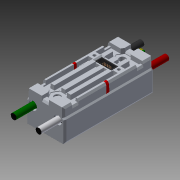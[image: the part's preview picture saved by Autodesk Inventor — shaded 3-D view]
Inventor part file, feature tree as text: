
AUTODESK INVENTOR PART (.ipt)
format: ipt  version: 2018 (Build 220112000, 112)  size: 3,547,136 bytes
history: native  units: in
note: dims shown in document units (in); Inventor stores cm internally (conversion verified against a paired STEP export)
features: plane x2, split x2, boolean_combine x1, imported_body x1
ambient origin geometry x8: Origin, YZ Plane, XZ Plane, XY Plane, X Axis, Y Axis, Z Axis, Center Point
bodies: Body1 (feature_tree)
feature tree (6):
  boolean_combine  "Combine11"
  plane  "Work Plane1"
  split  "Split1"
  plane  "Work Plane2"
  split  "Split2"
  imported_body  "Base1"
